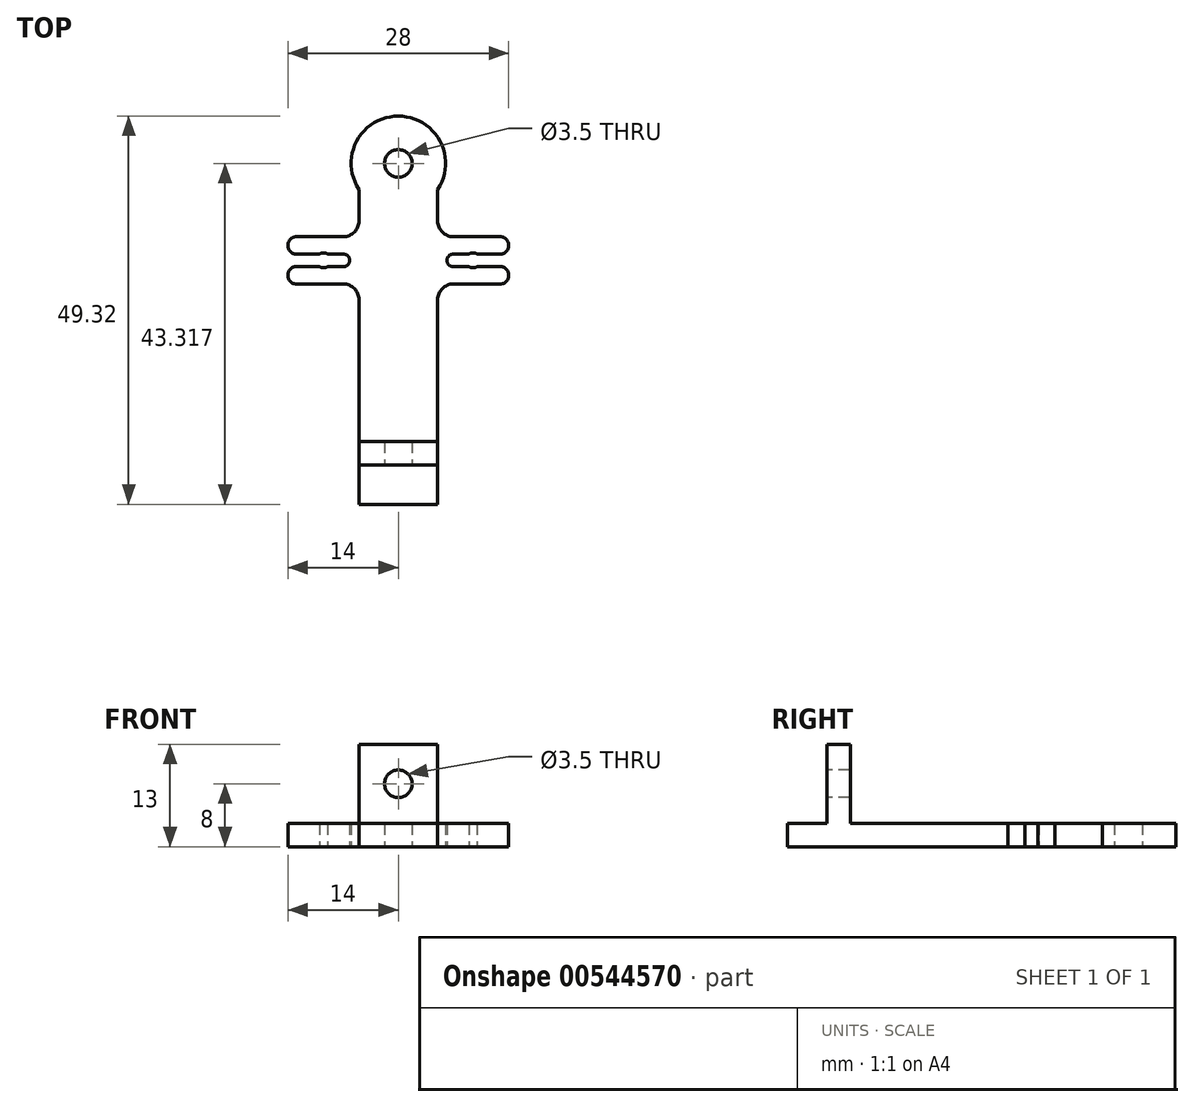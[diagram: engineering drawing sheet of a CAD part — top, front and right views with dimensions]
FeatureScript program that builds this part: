
annotation { "Feature Type Name" : "Feature", "Feature Type Description" : "" }
export const myFeature = defineFeature(function(context is Context, id is Id, definition is map)
    precondition{}
    {
        {
            var Q0;
            Q0=qCreatedBy(makeId("Top.planeOp"),FACE);
            var sketch = newSketch(context, id + "F0", { "sketchPlane" : qUnion([Q0])});
            skLineSegment(sketch, "E0", {"start": v(-5, 0) * mm, "end": v(-5, 26) * mm});
            skLineSegment(sketch, "E1", {"start": v(5, 40) * mm, "end": v(5, 36) * mm});
            skPoint(sketch, "E2.visualSharp", {"position": v(-5, 40) * mm});
            skLineSegment(sketch, "E3", {"start": v(5, 0) * mm, "end": v(5, 0) * mm});
            skPoint(sketch, "E4.visualSharp", {"position": v(5, 0) * mm});
            skArc(sketch, "E5", {"start": v(5, 40) * mm, "mid": v(0, 49.32) * mm, "end": v(-5, 40) * mm});
            skCircle(sketch, "E6", {"center": v(0, 43.32) * mm, "radius": 1.75 * mm});
            skLineSegment(sketch, "E7", {"start": v(-5, 0) * mm, "end": v(5, 0) * mm});
            skLineSegment(sketch, "E8.bottom", {"start": v(7, 34) * mm, "end": v(13, 34) * mm});
            skLineSegment(sketch, "E8.top", {"start": v(7, 28) * mm, "end": v(13, 28) * mm});
            skLineSegment(sketch, "E8.right", {"start": v(14, 33) * mm, "end": v(14, 32.8) * mm});
            skArc(sketch, "E9", {"start": v(10, 31.8) * mm, "mid": v(9.49, 31.95) * mm, "end": v(8.98, 31.8) * mm});
            skPoint(sketch, "E10", {"position": v(14, 31) * mm});
            skLineSegment(sketch, "E11", {"start": v(10, 31.8) * mm, "end": v(13, 31.8) * mm});
            skLineSegment(sketch, "E12", {"start": v(10, 30.2) * mm, "end": v(13, 30.2) * mm});
            skLineSegment(sketch, "E13.trimOffspring", {"start": v(14, 29.2) * mm, "end": v(14, 29) * mm});
            skPoint(sketch, "E14.visualSharp", {"position": v(14, 31.8) * mm});
            skArc(sketch, "E14.filletArc", {"start": v(13, 31.8) * mm, "mid": v(13.7, 32.1) * mm, "end": v(14, 32.8) * mm});
            skPoint(sketch, "E15.visualSharp", {"position": v(14, 30.2) * mm});
            skArc(sketch, "E15.filletArc", {"start": v(14, 29.2) * mm, "mid": v(13.7, 29.9) * mm, "end": v(13, 30.2) * mm});
            skPoint(sketch, "E16.visualSharp", {"position": v(14, 34) * mm});
            skArc(sketch, "E16.filletArc", {"start": v(14, 33) * mm, "mid": v(13.7, 33.7) * mm, "end": v(13, 34) * mm});
            skPoint(sketch, "E17.visualSharp", {"position": v(14, 28) * mm});
            skArc(sketch, "E17.filletArc", {"start": v(13, 28) * mm, "mid": v(13.7, 28.3) * mm, "end": v(14, 29) * mm});
            skLineSegment(sketch, "E18.bottom", {"start": v(8.98, 31.8) * mm, "end": v(6.98, 31.8) * mm});
            skLineSegment(sketch, "E18.top", {"start": v(8.98, 30.2) * mm, "end": v(6.98, 30.2) * mm});
            skArc(sketch, "E19.trimOffspring", {"start": v(8.98, 30.2) * mm, "mid": v(9.49, 30.05) * mm, "end": v(10, 30.2) * mm});
            skArc(sketch, "E20", {"start": v(6.98, 31.8) * mm, "mid": v(6.18, 31) * mm, "end": v(6.98, 30.2) * mm});
            skLineSegment(sketch, "E21.trimOffspring", {"start": v(5, 26) * mm, "end": v(5, 0) * mm});
            skPoint(sketch, "E22.visualSharp", {"position": v(5, 34) * mm});
            skArc(sketch, "E22.filletArc", {"start": v(5, 36) * mm, "mid": v(5.59, 34.59) * mm, "end": v(7, 34) * mm});
            skPoint(sketch, "E23.visualSharp", {"position": v(5, 28) * mm});
            skArc(sketch, "E23.filletArc", {"start": v(7, 28) * mm, "mid": v(5.59, 27.41) * mm, "end": v(5, 26) * mm});
            skLineSegment(sketch, "E24", {"start": v(0, 0) * mm, "end": v(0, 43.32) * mm, "construction": true});
            skArc(sketch, "E25.MirrorCS", {"start": v(-5, 36) * mm, "mid": v(-5.59, 34.59) * mm, "end": v(-7, 34) * mm});
            skLineSegment(sketch, "E26.MirrorCS", {"start": v(-14, 29.2) * mm, "end": v(-14, 29) * mm});
            skLineSegment(sketch, "E27.MirrorCS", {"start": v(-7, 34) * mm, "end": v(-13, 34) * mm});
            skLineSegment(sketch, "E28.MirrorCS", {"start": v(-7, 28) * mm, "end": v(-13, 28) * mm});
            skLineSegment(sketch, "E29.MirrorCS", {"start": v(-14, 33) * mm, "end": v(-14, 32.8) * mm});
            skArc(sketch, "E30.MirrorCS", {"start": v(-10, 31.8) * mm, "mid": v(-9.49, 31.95) * mm, "end": v(-8.98, 31.8) * mm});
            skLineSegment(sketch, "E31.MirrorCS", {"start": v(-10, 30.2) * mm, "end": v(-13, 30.2) * mm});
            skArc(sketch, "E32.MirrorCS", {"start": v(-13, 31.8) * mm, "mid": v(-13.7, 32.1) * mm, "end": v(-14, 32.8) * mm});
            skArc(sketch, "E33.MirrorCS", {"start": v(-7, 28) * mm, "mid": v(-5.59, 27.41) * mm, "end": v(-5, 26) * mm});
            skArc(sketch, "E34.MirrorCS", {"start": v(-8.98, 30.2) * mm, "mid": v(-9.49, 30.05) * mm, "end": v(-10, 30.2) * mm});
            skLineSegment(sketch, "E35.MirrorCS", {"start": v(-8.98, 31.8) * mm, "end": v(-6.98, 31.8) * mm});
            skPoint(sketch, "E36.MirrorP", {"position": v(-14, 31) * mm});
            skArc(sketch, "E37.MirrorCS", {"start": v(-6.98, 31.8) * mm, "mid": v(-6.18, 31) * mm, "end": v(-6.98, 30.2) * mm});
            skPoint(sketch, "E38.MirrorP", {"position": v(-14, 28) * mm});
            skArc(sketch, "E39.MirrorCS", {"start": v(-14, 29.2) * mm, "mid": v(-13.7, 29.9) * mm, "end": v(-13, 30.2) * mm});
            skLineSegment(sketch, "E40.MirrorCS", {"start": v(-10, 31.8) * mm, "end": v(-13, 31.8) * mm});
            skLineSegment(sketch, "E41.MirrorCS", {"start": v(-8.98, 30.2) * mm, "end": v(-6.98, 30.2) * mm});
            skArc(sketch, "E42.MirrorCS", {"start": v(-14, 33) * mm, "mid": v(-13.7, 33.7) * mm, "end": v(-13, 34) * mm});
            skPoint(sketch, "E43.MirrorP", {"position": v(-14, 34) * mm});
            skArc(sketch, "E44.MirrorCS", {"start": v(-13, 28) * mm, "mid": v(-13.7, 28.3) * mm, "end": v(-14, 29) * mm});
            skPoint(sketch, "E45.MirrorP", {"position": v(-14, 30.2) * mm});
            skPoint(sketch, "E46.MirrorP", {"position": v(-14, 31.8) * mm});
            skLineSegment(sketch, "E47.trimOffspring", {"start": v(-5, 36) * mm, "end": v(-5, 40) * mm});
            skSolve(sketch);
        }
        {
            var Q0;
            Q0 = qSketchRegion(id + "F0", true);
            extrude(context, id + "F1", {"entities" : qUnion([Q0]), "depth" : 3 * mm, "offsetDistance" : 25 * mm});
        }
        {
            var Q0;
            Q0=makeQuery(id+"F1.opExtrude","CAP_FACE",FACE,{"disambiguationData":[OSD([sQuery(id+"F0.wireOp",EDGE,"jMgaTMJG-whsZ-hF9W-8lVc-IDnyIRAKOdKQ"),sQuery(id+"F0.wireOp",EDGE,"KVwl3TS2-dFXs-bdL4-JWQN-v48CK5vIZmfp"),sQuery(id+"F0.wireOp",EDGE,"E0"),sQuery(id+"F0.wireOp",EDGE,"B8GZw9FT-YHi4-N2Wj-fHo7-l5hUcQFd2fOV"),sQuery(id+"F0.wireOp",EDGE,"E1"),sQuery(id+"F0.wireOp",EDGE,"E2.filletArc"),sQuery(id+"F0.wireOp",EDGE,"8ca38678-3127-4656-982e-766f12863705.filletArc"),sQuery(id+"F0.wireOp",EDGE,"E3"),sQuery(id+"F0.wireOp",EDGE,"E4.filletArc"),sQuery(id+"F0.wireOp",EDGE,"afdf545f-bcca-47d8-bd32-12c39119ae1b.filletArc")])],"isStart":false});
            var sketch = newSketch(context, id + "F2", { "sketchPlane" : qUnion([Q0])});
            skLineSegment(sketch, "E48.bottom", {"start": v(-5, 8) * mm, "end": v(5, 8) * mm});
            skLineSegment(sketch, "E48.top", {"start": v(-5, 5) * mm, "end": v(5, 5) * mm});
            skLineSegment(sketch, "E48.left", {"start": v(-5, 8) * mm, "end": v(-5, 5) * mm});
            skLineSegment(sketch, "E48.right", {"start": v(5, 8) * mm, "end": v(5, 5) * mm});
            skSolve(sketch);
        }
        {
            var Q0;
            Q0=makeQuery(id+"F2.imprint","IMPRINT",FACE,{"disambiguationData":[TD([[makeQuery(id+"F2.imprint","IMPRINT",EDGE,{"derivedFrom":sQuery(id+"F2.wireOp",EDGE,"E48.bottom")}),-1.0]])]});
            extrude(context, id + "F3", {"entities" : qUnion([Q0]), "operationType" : NewBodyOperationType.ADD, "depth" : 10 * mm, "offsetDistance" : 25 * mm});
        }
        {
            var Q0;
            Q0=makeQuery(id+"F3.opExtrude","SWEPT_FACE",FACE,{"disambiguationData":[OSD([sQuery(id+"F2.wireOp",EDGE,"E48.top")])]});
            var sketch = newSketch(context, id + "F4", { "sketchPlane" : qUnion([Q0])});
            skCircle(sketch, "E49", {"center": v(0, 8) * mm, "radius": 1.75 * mm});
            skPoint(sketch, "E49.centerSnap0", {"position": v(0, 3) * mm});
            skSolve(sketch);
        }
        {
            var Q0;
            Q0=makeQuery(id+"F4.imprint","IMPRINT",FACE,{"disambiguationData":[TD([[makeQuery(id+"F4.imprint","IMPRINT",EDGE,{"derivedFrom":sQuery(id+"F4.wireOp",EDGE,"E49")}),1.0]])]});
            extrude(context, id + "F5", {"entities" : qUnion([Q0]), "operationType" : NewBodyOperationType.REMOVE, "endBound" : BoundingType.THROUGH_ALL, "oppositeDirection" : true, "depth" : 25 * mm, "offsetDistance" : 25 * mm});
        }
    });
